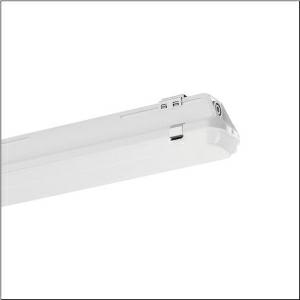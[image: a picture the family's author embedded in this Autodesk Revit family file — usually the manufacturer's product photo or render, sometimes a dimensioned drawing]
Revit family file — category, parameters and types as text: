
# Revit family: monsun_r__11_51fp20mp4b0u_7a3b
name_source: partatom
category: Lighting Fixtures
units: mm (PartAtom-declared; Revit-internal decimal feet)

## family parameters
Cut with Voids When Loaded = No
Host = Face
Light Source = No
Part Type = Normal
Room Calculation Point = No
Round Connector Dimension = Use Diameter
Shared = No

## types (1)
- --- (1 x LED, 10910 lm, 62.4 W, 4000K)
    Apparent Load = 62 VA
    CIE Flux Codes = 45 75 93 94 100
    Color Rendering = 80
    Color Temperature = 4000K
    Default Elevation = 1800 mm
    Description = Monsun® 11, damp-proof luminaire, chain hanger, primary optical cover: enclosure, of PC, light emission: direct distribution, primary light characteristic: symmetric, installation type: suspended mounting, surface-mounted, horizontal mounting, vertical mounting, LED, rated luminous flux: 10.910lm, luminous efficacy: 175lm/W, light colour: 840, colour temperature: 4000K, control gear: ON/OFF Multilumen, with terminal, 3-pole, max. 2.5mm², mains connection: 220..240V, AC, 50/60Hz, rated input power: 62W, luminaire housing, of glass-fibre reinforced polyester, uncoated, bright grey, incl. chain hanger, length: 1.590mm, width: 90mm, height: 88mm, clip for enclosure, of stainless steel (V2A), ceiling mounting element, of stainless steel (V2A), chain hanger, of stainless steel (V2A), protection rating (complete): IP66, insulation class (complete): insulation class I (protective earthing), certification: CE, ENEC, VDE, UKCA, protection symbol: D, impact resistance: IK08, permissible operating ambient temperature: -35..+35°C, standard: EN 50419, EN 60598-2-1, contact your sales advisor before using the luminaires in applications with unclear chemical exposure, large temperature fluctuations or condensation-forming humidity, LABS conformity tested according to VDMA 24364:2018-05, no direct snow, no direct sun, no direct rain, for indoor or canopied outdoor use, corresponds to IFS (International Featured Standards) requirements for safety and quality in the food industry, packaging unit: 1 piece
    Height = 89 mm
    Lamp = 1 x LED
    Lamp Light Flux = 10910 lm
    Lamp Power = 62.4 W
    Lamp count = 1
    Length = 1590 mm
    Luminous efficacy = 175 lm/W
    Manufacturer = Siteco
    ModVariant = No
    Model = 51FP20MP4B0U
    Mounting Place = Ceiling
    Mounting Type = Surface mounted
    Number of Poles = 1
    OnlyDefault = Yes
    Power Factor = 1
    Product Name = Monsun® 11
    Product group = damp-proof luminaire
    ProductGroupID = 301
    Protection Class = Protection class I
    Protection Degree = IP 66
    RLX_Detail_Level = 1
    RLX_Emergency_Light_Flux = 0 lm
    RLX_Emergency_Type = 0
    RLX_Emergency_Type_DB = No
    RlxData = <blob elided: 89833 chars, md5=361257bb>
    Socket = socket
    Standby Power = 0 W
    System Light Flux = 10910 lm
    System Power = 62 W
    Type Comments = factory setting: luminous flux: 100 % | (A | C | E) | 147 mA
    Type Image = l_1349237.jpg
    URL = http://relux.com
    VarID = @adj_041165
    Voltage = 0 V
    Weight = 0.00 kg
    Width = 90 mm

## geometry (parser evidence)
native form markers: Blend x4, Sweep x14
no freeform markers — native parametric forms only
